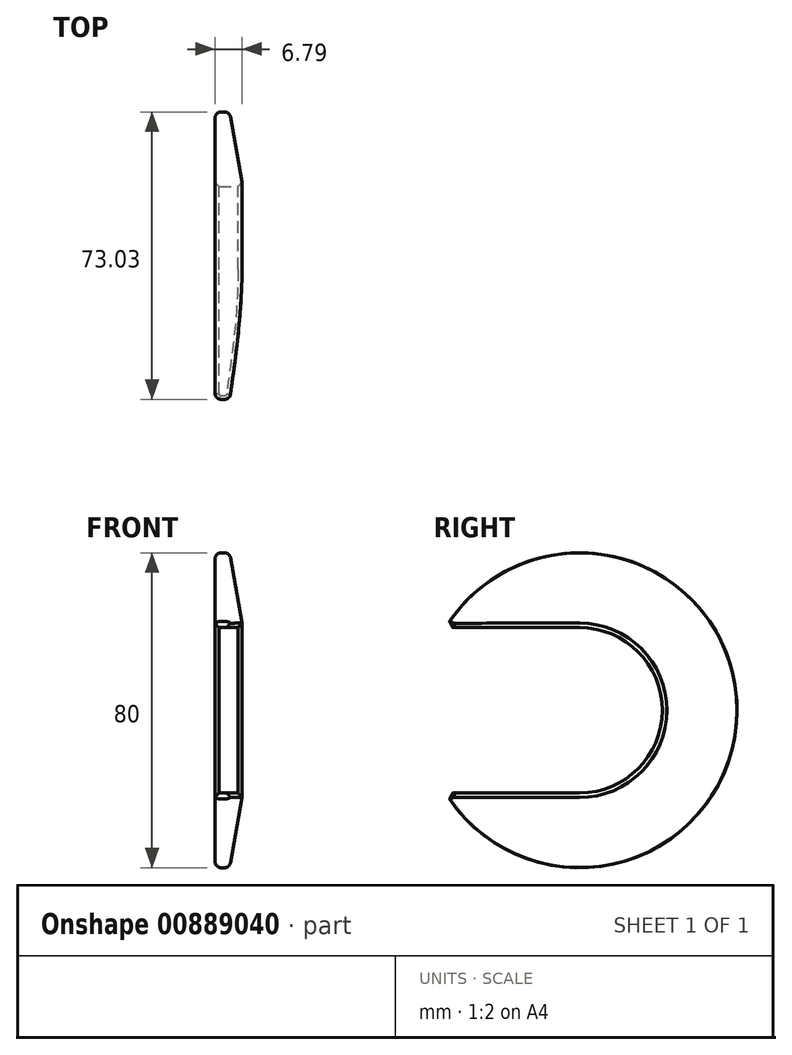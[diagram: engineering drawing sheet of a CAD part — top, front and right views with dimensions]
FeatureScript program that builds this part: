
annotation { "Feature Type Name" : "Feature", "Feature Type Description" : "" }
export const myFeature = defineFeature(function(context is Context, id is Id, definition is map)
    precondition{}
    {
        {
            var Q0;
            Q0=qCreatedBy(makeId("Front.planeOp"),FACE);
            var sketch = newSketch(context, id + "F0", { "sketchPlane" : qUnion([Q0])});
            skLineSegment(sketch, "E0", {"start": v(0, 0) * mm, "end": v(0, 21) * mm, "construction": true});
            skLineSegment(sketch, "E1", {"start": v(-3.35, 40) * mm, "end": v(0, 21) * mm});
            skLineSegment(sketch, "E2", {"start": v(-3.35, 40) * mm, "end": v(-7, 40) * mm});
            skLineSegment(sketch, "E3", {"start": v(-7, 40) * mm, "end": v(-7, 21) * mm});
            skLineSegment(sketch, "E4", {"start": v(-7, 21) * mm, "end": v(0, 21) * mm});
            skLineSegment(sketch, "E5", {"start": v(0, 0) * mm, "end": v(-22.75, 0) * mm, "construction": true});
            skSolve(sketch);
        }
        {
            var Q0;
            Q0=makeQuery(id+"F0.imprint","IMPRINT",FACE,{"disambiguationData":[TD([[makeQuery(id+"F0.imprint","IMPRINT",EDGE,{"derivedFrom":sQuery(id+"F0.wireOp",EDGE,"E1")}),-1.0]])]});
            var Q1;
            Q1=sQuery(id+"F0.wireOp",EDGE,"E5");
            revolve(context, id + "F1", {"surfaceOperationType" : NewSurfaceOperationType.NEW, "entities" : qUnion([Q0]), "axis" : qUnion([Q1]), "revolveType" : RevolveType.FULL});
        }
        {
            var Q0;
            {var subQ0=sQuery(id+"F0.wireOp",EDGE,"E3");var subQ1=sQuery(id+"F0.wireOp",EDGE,"E4");Q0=makeQuery(id+"FrV02xwoEvqWM6H_1.boolean.opBoolean","SPLIT",EDGE,{"disambiguationData":[TD([makeQuery(id+"FrV02xwoEvqWM6H_1.opExtrude","SWEPT_FACE",FACE,{"disambiguationData":[OSD([sQuery(id+"FEZhr92aBguRhcM_1.wireOp",EDGE,"02acfb92-cffa-4e55-be06-1235d483ef04.left")])]})])],"derivedFrom":makeQuery(id+"F1.opRevolve","SWEPT_EDGE",EDGE,{"disambiguationData":[OSD([subQ0,subQ1])]})});}
            var Q1;
            {var subQ0=sQuery(id+"F0.wireOp",EDGE,"E3");var subQ1=sQuery(id+"F0.wireOp",EDGE,"E4");Q1=makeQuery(id+"FrV02xwoEvqWM6H_1.boolean.opBoolean","SPLIT",EDGE,{"disambiguationData":[TD([makeQuery(id+"FrV02xwoEvqWM6H_1.opExtrude","SWEPT_FACE",FACE,{"disambiguationData":[OSD([sQuery(id+"FEZhr92aBguRhcM_1.wireOp",EDGE,"449b8a49-b048-4c21-ae6e-c1fcfaef5a71.right")])]})])],"derivedFrom":makeQuery(id+"F1.opRevolve","SWEPT_EDGE",EDGE,{"disambiguationData":[OSD([subQ0,subQ1])]})});}
            var Q2;
            {var subQ0=sQuery(id+"F0.wireOp",EDGE,"E3");var subQ1=sQuery(id+"F0.wireOp",EDGE,"E4");Q2=makeQuery(id+"FrV02xwoEvqWM6H_1.boolean.opBoolean","SPLIT",EDGE,{"disambiguationData":[TD([makeQuery(id+"FrV02xwoEvqWM6H_1.opExtrude","SWEPT_FACE",FACE,{"disambiguationData":[OSD([sQuery(id+"FEZhr92aBguRhcM_1.wireOp",EDGE,"60076664-aa62-4bfb-94f7-0ca028c82a79.1.0")])]})])],"derivedFrom":makeQuery(id+"F1.opRevolve","SWEPT_EDGE",EDGE,{"disambiguationData":[OSD([subQ0,subQ1])]})});}
            var Q3;
            {var subQ0=sQuery(id+"F0.wireOp",EDGE,"E3");var subQ1=sQuery(id+"F0.wireOp",EDGE,"E4");Q3=makeQuery(id+"FrV02xwoEvqWM6H_1.boolean.opBoolean","SPLIT",EDGE,{"disambiguationData":[TD([makeQuery(id+"FrV02xwoEvqWM6H_1.opExtrude","SWEPT_FACE",FACE,{"disambiguationData":[OSD([sQuery(id+"FEZhr92aBguRhcM_1.wireOp",EDGE,"60076664-aa62-4bfb-94f7-0ca028c82a79.2.0")])]})])],"derivedFrom":makeQuery(id+"F1.opRevolve","SWEPT_EDGE",EDGE,{"disambiguationData":[OSD([subQ0,subQ1])]})});}
            chamfer(context, id + "F2", {"entities" : qUnion([Q0, Q1, Q2, Q3]), "width" : 1 * mm, "tangentPropagation" : true});
        }
        {
            var Q0;
            Q0=makeQuery(id+"F1.opRevolve","SWEPT_EDGE",EDGE,{"disambiguationData":[OSD([sQuery(id+"F0.wireOp",EDGE,"E1"),sQuery(id+"F0.wireOp",EDGE,"E2")])]});
            var Q1;
            Q1=makeQuery(id+"F1.opRevolve","SWEPT_EDGE",EDGE,{"disambiguationData":[OSD([sQuery(id+"F0.wireOp",EDGE,"E2"),sQuery(id+"F0.wireOp",EDGE,"E3")])]});
            fillet(context, id + "F3", {"entities" : qUnion([Q0, Q1]), "radius" : 1.5 * mm, "tangentPropagation" : true, "allowEdgeOverflow" : false});
        }
        {
            var Q0;
            Q0=qCreatedBy(makeId("Right.planeOp"),FACE);
            var sketch = newSketch(context, id + "F4", { "sketchPlane" : qUnion([Q0])});
            skLineSegment(sketch, "E6.bottom", {"start": v(0, -21) * mm, "end": v(-61.79, -21) * mm});
            skLineSegment(sketch, "E6.top", {"start": v(0, 21) * mm, "end": v(-61.79, 21) * mm});
            skLineSegment(sketch, "E6.left", {"start": v(0, -21) * mm, "end": v(0, 21) * mm});
            skLineSegment(sketch, "E6.right", {"start": v(-61.79, -21) * mm, "end": v(-61.79, 21) * mm});
            skSolve(sketch);
        }
        {
            var Q0;
            Q0=makeQuery(id+"F4.imprint","IMPRINT",FACE,{"disambiguationData":[TD([[makeQuery(id+"F4.imprint","IMPRINT",EDGE,{"derivedFrom":sQuery(id+"F4.wireOp",EDGE,"E6.bottom")}),-1.0]])]});
            extrude(context, id + "F5", {"entities" : qUnion([Q0]), "operationType" : NewBodyOperationType.REMOVE, "oppositeDirection" : true, "depth" : 25 * mm, "offsetDistance" : 25 * mm});
        }
        {
            var Q0;
            Q0=makeQuery(id+"F5.boolean.opBoolean","INTERSECT",EDGE,{"derivedFrom":[makeQuery(id+"F1.opRevolve","SWEPT_FACE",FACE,{"disambiguationData":[OSD([sQuery(id+"F0.wireOp",EDGE,"E3")])]}),makeQuery(id+"F5.opExtrude","SWEPT_FACE",FACE,{"disambiguationData":[OSD([sQuery(id+"F4.wireOp",EDGE,"E6.top")])]})]});
            var Q1;
            Q1=makeQuery(id+"F5.boolean.opBoolean","INTERSECT",EDGE,{"derivedFrom":[makeQuery(id+"F1.opRevolve","SWEPT_FACE",FACE,{"disambiguationData":[OSD([sQuery(id+"F0.wireOp",EDGE,"E3")])]}),makeQuery(id+"F5.opExtrude","SWEPT_FACE",FACE,{"disambiguationData":[OSD([sQuery(id+"F4.wireOp",EDGE,"E6.bottom")])]})]});
            chamfer(context, id + "F6", {"entities" : qUnion([Q0, Q1]), "width" : 1 * mm, "tangentPropagation" : true});
        }
    });
